# Revit family: PRD_FrankeWS_WstBns_RodanWasteBin_RODX605,605S,607
name_source: partatom
category: Furniture
revit_build: Autodesk Revit 2018 (Build: 20190510_1515(x64)
units: mm (PartAtom-declared; Revit-internal decimal feet)

## family parameters
Cut with Voids When Loaded = No
Host = Face
OmniClass Number = 23.40.20.31.11
OmniClass Title = Bins
Room Calculation Point = No
Shared = No

## types (3) — shared parameters
AssetType = Fixed
Category = Pr_40_50_07_96, Waste bins
Color = Stainless steel
Default Elevation = 820 mm  [stored 2.69029 ft]
DurationUnit = year
Finish = Satin finished
FinishAndColour = Stainless steel, satin finished
Form = Wall mounted
IfcExportAs = IfcFurnitureType
IfcExportType = NOTDEFINED
IntegralAccessories = includes mounting materials
Lock = no lock
MainColor = Stainless steel
Manufacturer = KWC Group AG
ManufacturerName = KWC Group AG
ManufacturerURL = www.kwc.com
Material = Stainless steel
Materials = Stainless steel 1.4301
NBSDescription = Waste bins
NBSReference = 45-35-72/380
ProductInformation = https://pim.kwc.com
Style = Waste bin
URL = www.kwc.com
Uniclass2015Code = Pr_40_50_07_96
Uniclass2015Title = Waste bins
Uniclass2015Version = Products v1.10
Version = 1
WarrantyDurationUnit = year
WasteBinMaterial = PRD_AR_StainlessSteel_SatinFinished

## per-type parameters (varying)
| type | BIMObjectName | BagHolder | Description | Features | FillingVolume | GrossWeight | Lid | ModelNumber | Name | NetWeight | NominalDepth | NominalHeight | NominalWidth | OverallDepth | OverallHeight | Size | TypeOfBagHolder |
| RODX605 | PRD_AR_WasteBins_RodanWasteBin_RODX605 | No | Waste bin for wall mounting, stainless steel, surface satin finished, material thickness 0.8 mm, rounded edges, mounting either with mounting bracket or directly onto the wall, incl. stainless steel screws and dowels. capacity: approx. 23 liter | stainless steel, 0.80 mm, satin finished, wall mounting, 355x460x168 mm (WxHxD) | 23.00 l | 4.90 kg | no | 2000090061 | RODAN Waste bin RODX605 | 4.50 kg | 168 mm  [stored 0.551181 ft] | 460 mm  [stored 1.50919 ft] | 355 mm  [stored 1.1647 ft] | 168 mm  [stored 0.551181 ft] | 460 mm  [stored 1.50919 ft] | 355x460x168 mm | PRD_AR_WlMntdFrntrSpprtRls_BagHolderE-RODX605N,E-RODX607 : E-RODX605N |
| RODX607 | PRD_AR_WasteBins_RodanWasteBin_RODX607 | Yes | Waste bin for wall mounting, stainless steel, surface satin finished, material thickness 0.8 mm, rounded edges, mounting either with
mounting bracket or directly onto the wall, incl. stainless steel screws and dowels. Capacity: approx. 60 liter | stainless steel, 0.80 mm, satin finished, wall mounting, 480x620x210 mm (WxHxD) | 60.00 l | 8.00 kg | optional | 2000101351 | RODAN Waste bin RODX607 | 6.69 kg | 210 mm  [stored 0.688976 ft] | 620 mm  [stored 2.03412 ft] | 480 mm  [stored 1.5748 ft] | 210 mm  [stored 0.688976 ft] | 620 mm  [stored 2.03412 ft] | 480x620x210 mm | PRD_AR_WlMntdFrntrSpprtRls_BagHolderE-RODX605N,E-RODX607 : E-RODX607 |
| RODX605S | PRD_AR_WasteBins_RodanWasteBin_RODX605S | No | Waste bin for wall mounting, stainless steel, surface satin finished, material thickness 0.8 mm, rounded edges, mounting either with
mounting bracket or directly onto the wall, incl. stainless steel screws and dowels. Capacity: approx. 18 liter | stainless steel, 0.80 mm, satin finished, wall mounting, 275x460x177 mm (WxHxD) | 18.00 l | 4.40 kg | no | 2000101236 | RODAN Waste bin RODX605S | 3.90 kg | 177 mm  [stored 0.580709 ft] | 460 mm  [stored 1.50919 ft] | 275 mm | 177 mm  [stored 0.580709 ft] | 460 mm  [stored 1.50919 ft] | 275x460x177 mm | PRD_AR_WlMntdFrntrSpprtRls_BagHolderE-RODX605N,E-RODX607 : E-RODX605N |

note: column(s) folded — value = type name in every type: Model, ModelReference

note: [stored X ft] marks values corroborated as IEEE doubles in the binary element streams (Revit-internal decimal feet)

## geometry (parser evidence)
native form markers: Sweep x3
no freeform markers — native parametric forms only
